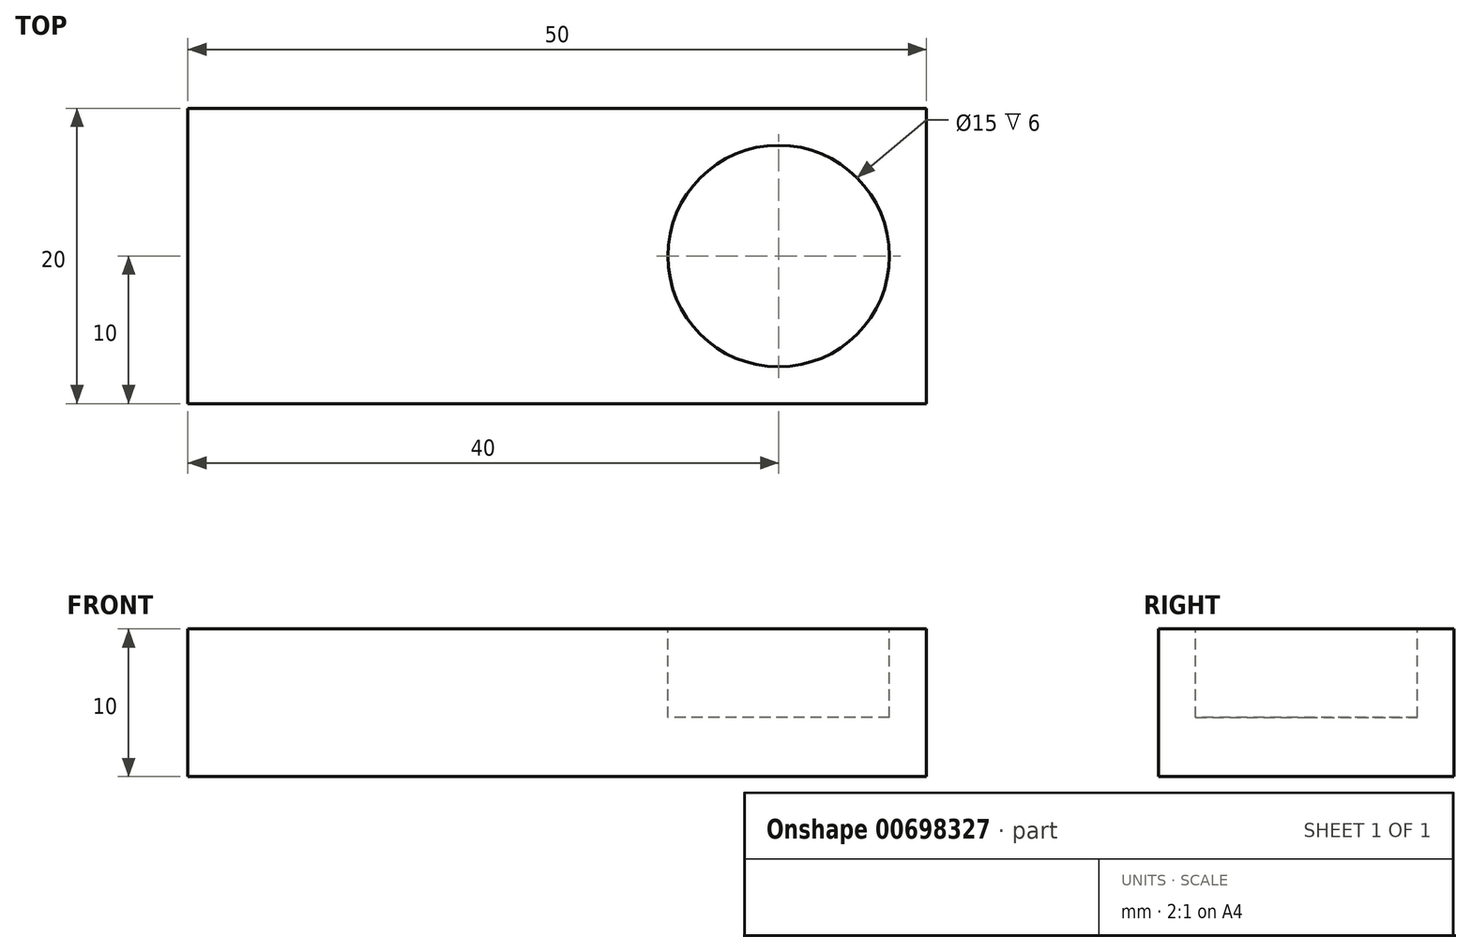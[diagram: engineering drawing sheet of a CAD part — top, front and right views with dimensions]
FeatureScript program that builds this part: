
annotation { "Feature Type Name" : "Feature", "Feature Type Description" : "" }
export const myFeature = defineFeature(function(context is Context, id is Id, definition is map)
    precondition{}
    {
        {
            var Q0;
            Q0=qCreatedBy(makeId("Top.planeOp"),FACE);
            var sketch = newSketch(context, id + "F0", { "sketchPlane" : qUnion([Q0])});
            skLineSegment(sketch, "E0.bottom", {"start": v(-40, 10) * mm, "end": v(10, 10) * mm});
            skLineSegment(sketch, "E0.top", {"start": v(-40, -10) * mm, "end": v(10, -10) * mm});
            skLineSegment(sketch, "E0.left", {"start": v(-40, 10) * mm, "end": v(-40, -10) * mm});
            skLineSegment(sketch, "E0.right", {"start": v(10, 10) * mm, "end": v(10, -10) * mm});
            skSolve(sketch);
        }
        {
            var Q0;
            Q0 = qSketchRegion(id + "F0", true);
            extrude(context, id + "F1", {"entities" : qUnion([Q0]), "endBound" : BoundingType.SYMMETRIC, "depth" : 10 * mm, "offsetDistance" : 25 * mm});
        }
        {
            var Q0;
            Q0=makeQuery(id+"F1.opExtrude","CAP_FACE",FACE,{"disambiguationData":[OSD([sQuery(id+"F0.wireOp",EDGE,"E0.bottom"),sQuery(id+"F0.wireOp",EDGE,"E0.top"),sQuery(id+"F0.wireOp",EDGE,"E0.left"),sQuery(id+"F0.wireOp",EDGE,"E0.right")])],"isStart":false});
            var sketch = newSketch(context, id + "F2", { "sketchPlane" : qUnion([Q0])});
            skCircle(sketch, "E1", {"center": v(0, 0) * mm, "radius": 7.5 * mm});
            skSolve(sketch);
        }
        {
            var Q0;
            Q0 = qSketchRegion(id + "F2", true);
            extrude(context, id + "F3", {"entities" : qUnion([Q0]), "operationType" : NewBodyOperationType.REMOVE, "oppositeDirection" : true, "depth" : 6 * mm, "offsetDistance" : 25 * mm});
        }
    });
